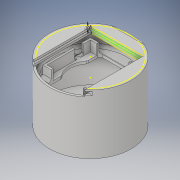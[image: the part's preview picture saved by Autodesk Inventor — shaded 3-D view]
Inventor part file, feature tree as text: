
AUTODESK INVENTOR PART (.ipt)
format: ipt  version: 2019 (Build 230136000, 136)  size: 531,456 bytes
history: native  units: in
note: dims shown in document units (in); Inventor stores cm internally (conversion verified against a paired STEP export)
features: sketch x23, extrude x16, fillet x12, plane x3, chamfer x1
ambient origin geometry x8: Origin, YZ Plane, XZ Plane, XY Plane, X Axis, Y Axis, Z Axis, Center Point
bodies: Solid1 (feature_tree)
feature tree (55):
  extrude  "Extrusion1"  Depth=3.737in
  extrude  "Extrusion2"  Depth=1.0in
  extrude  "Extrusion3"  Depth=0.125in
  extrude  "Extrusion4"  Depth=0.125in
  extrude  "Extrusion5"  Depth=0.1in
  plane  "Work Plane1"
  sketch  "Sketch6"  dims[d13=0.1in]
  chamfer  "Chamfer1"  Distance=0.5in
  extrude  "Extrusion8"  Depth=0.5in TaperAngle=0.0deg
  fillet  "Fillet1"  Radius=0.792in
  fillet  "Fillet2"  Radius=0.575in
  fillet  "Fillet3"  Radius=0.125in
  fillet  "Fillet4"  Radius=0.2in
  fillet  "Fillet5"  Radius=0.2in
  fillet  "Fillet6"  Radius=0.025in
  fillet  "Fillet10"  Radius=0.025in
  extrude  "Extrusion9"  Depth=0.025in
  sketch  "Sketch11"  dims[d16=1.45in]
  extrude  "Extrusion10"  Depth=0.225in
  extrude  "Extrusion11"  Depth=0.3in TaperAngle=0.0deg
  sketch  "Sketch13"  dims[d20=0.175in d21=0.5in d22=0.0in d23=0.792in]
  sketch  "Sketch14"  dims[d39=0.25in d40=0.125in d41=45.0deg d48=0.575in d49=0.0in d50=0.125in d51=0.2in d52=0.2in d53=0.025in d54=0.025in]
  sketch  "Sketch15"  dims[d55=0.025in d56=0.025in]
  extrude  "Extrusion12"  Depth=0.3in TaperAngle=0.0deg
  extrude  "Extrusion13"  Depth=0.094in TaperAngle=0.0deg
  fillet  "Fillet12"  Radius=0.1in
  fillet  "Fillet13"  Radius=0.094in
  plane  "Work Plane2"
  extrude  "Extrusion14"  Depth=0.05in
  extrude  "Extrusion15"  Depth=0.102in TaperAngle=0.0deg
  sketch  "Sketch19"  dims[d70=0.1in d71=0.094in d72=0.0in d73=0.1in d74=0.094in d75=0.0in]
  extrude  "Extrusion16"  Depth=0.25in
  extrude  "Extrusion17"  Depth=0.25in
  fillet  "Fillet15"  Radius=0.032in
  plane  "Work Plane3"
  fillet  "Fillet16"  Radius=0.044in
  extrude  "Extrusion18"  Depth=0.3in TaperAngle=0.0deg
  sketch  "Sketch23"  dims[d86=0.25in d87=0.25in d88=0.032in d89=0.044in]
  sketch  "Sketch24"  dims[d90=0.044in d91=0.3in d92=0.0in d93=0.3in]
  sketch  "Sketch25"  dims[d94=0.3in d95=0.7375in d96=0.0in d97=0.3in d98=180.0deg d99=0.3in d100=0.7375in d101=0.0in d102=0.125in d103=0.17in d104=0.0625in d105=0.04in d106=0.0in d107=0.125in]
  fillet  "Fillet17"  Radius=0.3in
  sketch  "Sketch1"  dims[d0=3.937in d1=3.737in]
  sketch  "Sketch2"  dims[d2=2.0in d3=0.0in d4=1.0in]
  sketch  "Sketch3"  dims[d5=0.125in d6=0.0in d7=2.0in]
  sketch  "Sketch4"  dims[d8=0.125in d9=0.0in d10=2.15in]
  sketch  "Sketch5"  dims[d11=2.05in d12=0.1in]
  sketch  "Sketch9"  dims[d14=0.1in]
  sketch  "Sketch10"  dims[d15=0.1in]
  sketch  "Sketch12"  dims[d17=0.35in d18=0.5in d19=0.0in]
  sketch  "Sketch16"  dims[d57=0.025in d61=0.225in]
  sketch  "Sketch17"  dims[d63=2.5in d64=0.3in d65=0.0in]
  sketch  "Sketch18"  dims[d66=0.3in d67=0.0in d68=0.3in d69=0.0in]
  sketch  "Sketch20"  dims[d76=0.05in d77=0.05in]
  sketch  "Sketch21"  dims[d78=1.25in d79=0.102in d80=0.0in]
  sketch  "Sketch22"  dims[d83=0.8in d85=0.25in]
